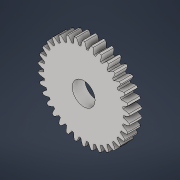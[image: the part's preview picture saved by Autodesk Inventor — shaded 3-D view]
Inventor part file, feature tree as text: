
AUTODESK INVENTOR PART (.ipt)
format: ipt  version: 2021 (Build 250183000, 183)  size: 308,224 bytes
history: native  units: mm (DEFAULTED — no unit token found)
features: plane x3, other x3, sketch x3, extrude x2
ambient origin geometry x8: Origin, YZ Plane, XZ Plane, XY Plane, X Axis, Y Axis, Z Axis, Center Point
bodies: Solid1 (feature_tree)
feature tree (11):
  extrude  "Extrusion1"  Depth=0.5mm TaperAngle=0.0deg
  plane  "Work Plane2"
  plane  "Work Plane8"
  plane  "Work Plane9"
  other  "Engrenagem reta"
  extrude  "Extrusão2"  Depth=10.0mm TaperAngle=0.0deg
  sketch  "Sketch1"  dims[d0=3.6mm d1=0.5mm d2=0.0mm]
  sketch  "Sketch2"  dims[d3=3.4mm d4=10.0mm d5=0.0mm]
  other  "Srf1"
  sketch  "Esboço3"  dims[d16=3.0mm d17=0.0mm d34=0.923998mm d39=0.0mm d41=0.0mm d43=3.0mm d46=3.0mm d47=0.0mm d48=0.0mm d49=0.9mm d50=0.5mm d51=0.0mm]
  other  "Diâmetro do flanco"
